# Revit family: BIMLIB_КомплектыДляУличногоМонтажа_SIB_SHUFT
name_source: partatom
category: Оборудование
revit_build: Autodesk Revit 2017 (Build: 20170118_1100(x64)
units: mm (PartAtom-declared; Revit-internal decimal feet)

## family parameters
Всегда вертикально = Да
На основе рабочей плоскости = Нет
Общий = Нет
При загрузке вырезать с полостями = Нет
Размер круглого соединителя = Использовать диаметр
Тип детали = Вставляется
Точка расчета площади = Нет

## types (6) — shared parameters
ADSK_URL документации изделия = http://www.shuft.ru
ADSK_URL страницы изделия = http://www.shuft.ru
ADSK_Версия Revit = 2017
ADSK_Версия семейства = v.1
ADSK_Единица измерения = компл.
ADSK_Завод-изготовитель = ООО «Завод ВКО» марка SHUFT
ADSK_Классификация нагрузок = Прочее
ADSK_Количество фаз = 1
ADSK_Коэффициент мощности = 1
ADSK_Материал = BIMLIB_Сталь_SHUFT
ADSK_Напряжение = 230 В
BL_BIM library = https://bimlib.pro
IP Двигателя = IP44
URL = http://www.shuft.ru
Изготовитель = ООО «Завод ВКО» марка SHUFT
Климатическое исполнение = У2

## per-type parameters (varying)
| type | A | ADSK_Размер_Диаметр | ADSK_Размер_Длина | B | C | d | r | r1 |
| SIB 100 S | 318 мм | 100 мм | 318 мм | 316 мм | 307 мм | 100 мм | 50 мм | 51 мм |
| SIB 125 S | 318 мм | 125 мм | 318 мм | 316 мм | 307 мм | 125 мм | 63 мм | 63 мм |
| SIB 160 S | 340 мм | 160 мм | 340 мм | 402 мм | 397 мм | 160 мм | 80 мм | 81 мм |
| SIB 200 S | 340 мм | 200 мм | 340 мм | 402 мм | 397 мм | 200 мм | 100 мм | 101 мм |
| SIB 250 S | 340 мм | 250 мм | 340 мм | 402 мм | 397 мм | 250 мм | 125 мм | 126 мм |
| SIB 315 S | 398 мм | 315 мм | 398 мм | 472 мм | 465 мм | 315 мм | 158 мм | 158 мм |
